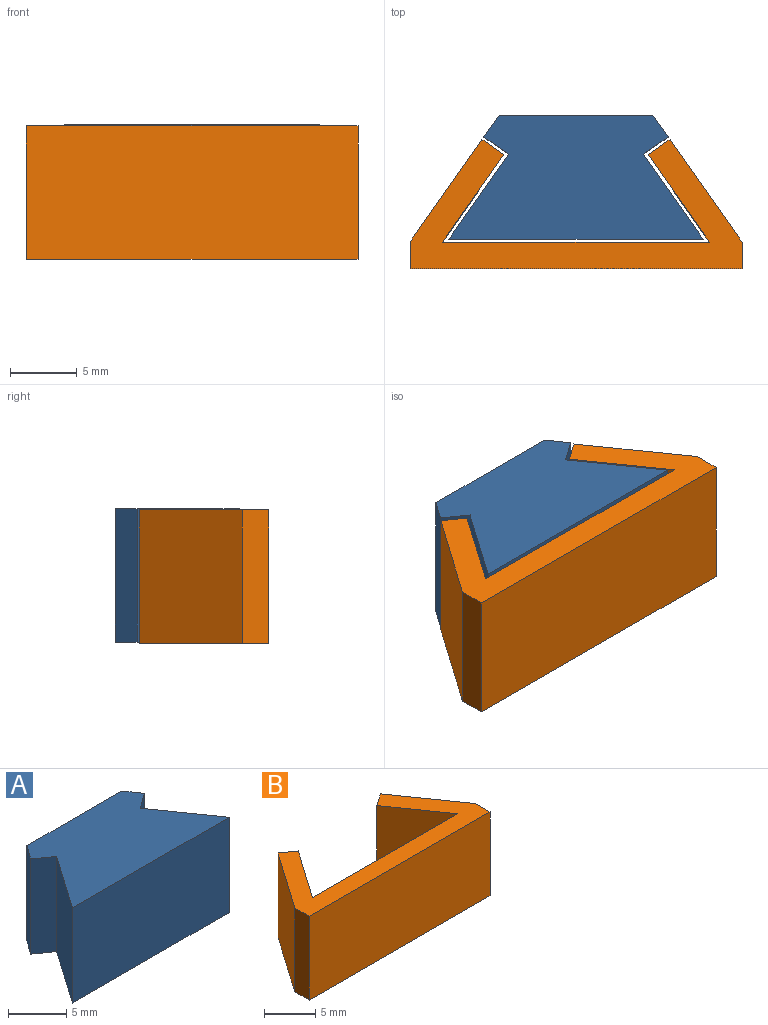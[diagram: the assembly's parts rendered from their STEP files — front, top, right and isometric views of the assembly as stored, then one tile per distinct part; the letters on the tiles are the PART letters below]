
ASSEMBLY  parts=2 mates=1
PART A: 10 faces, bbox 19x9.3x10 mm
  f0: plane 19.04x10mm, normal (0,-1,0), area 190.4mm2, adj f1,f7,f8,f9
  f1: plane 10x6.36mm, normal (0.82,0.57,0), area 77.7mm2, adj f0,f2,f8,f9
  f2: plane 10x1.84mm, normal (0.57,-0.82,0), area 22.5mm2, adj f1,f3,f8,f9
  f3: plane 10x1.64mm, normal (0.82,0.57,0), area 20mm2, adj f2,f4,f8,f9
  f4: plane 11.52x10mm, normal (0,1,0), area 115.2mm2, adj f3,f5,f8,f9
  f5: plane 10x1.64mm, normal (-0.82,0.57,0), area 20mm2, adj f4,f6,f8,f9
  f6: plane 10x1.84mm, normal (-0.57,-0.82,0), area 22.5mm2, adj f5,f7,f8,f9
  f7: plane 10x6.36mm, normal (-0.82,0.57,0), area 77.7mm2, adj f0,f6,f8,f9
  f8: plane 19.04x9.29mm, normal (0,0,1), area 129mm2, adj f0,f1,f2,f3,f4,f5,f6,f7
  f9: plane 19.04x9.29mm, normal (0,0,-1), area 129mm2, adj f0,f1,f2,f3,f4,f5,f6,f7
PART B: 12 faces, bbox 24.9x9.7x10 mm
  f0: plane 10x6.55mm, normal (0.82,-0.57,0), area 80mm2, adj f1,f9,f10,f11
  f1: plane 10x1.64mm, normal (0.57,0.82,0), area 20mm2, adj f0,f2,f10,f11
  f2: plane 10x7.7mm, normal (-0.82,0.57,0), area 94mm2, adj f1,f3,f10,f11
  f3: plane 10x2mm, normal (-1,0,0), area 20mm2, adj f2,f4,f10,f11
  f4: plane 24.88x10mm, normal (0,-1,0), area 248.8mm2, adj f3,f5,f10,f11
  f5: plane 10x2mm, normal (1,0,0), area 20mm2, adj f4,f6,f10,f11
  f6: plane 10x7.7mm, normal (0.82,0.57,0), area 94mm2, adj f5,f7,f10,f11
  f7: plane 10x1.64mm, normal (-0.57,0.82,0), area 20mm2, adj f6,f8,f10,f11
  f8: plane 10x6.55mm, normal (-0.82,-0.57,0), area 80mm2, adj f7,f9,f10,f11
  f9: plane 20x10mm, normal (0,1,0), area 200mm2, adj f0,f8,f10,f11
  f10: plane 24.88x9.7mm, normal (0,0,1), area 84.6mm2, adj f0,f1,f2,f3,f4,f5,f6,f7
  f11: plane 24.88x9.7mm, normal (0,0,-1), area 84.6mm2, adj f0,f1,f2,f3,f4,f5,f6,f7
PLACE A t=(0,-0.03,0.1)mm
PLACE B at identity fixed
MATE slider A.f8 <-> B.f10  axis (0,0,1) through (0,4.48,10.1)mm
